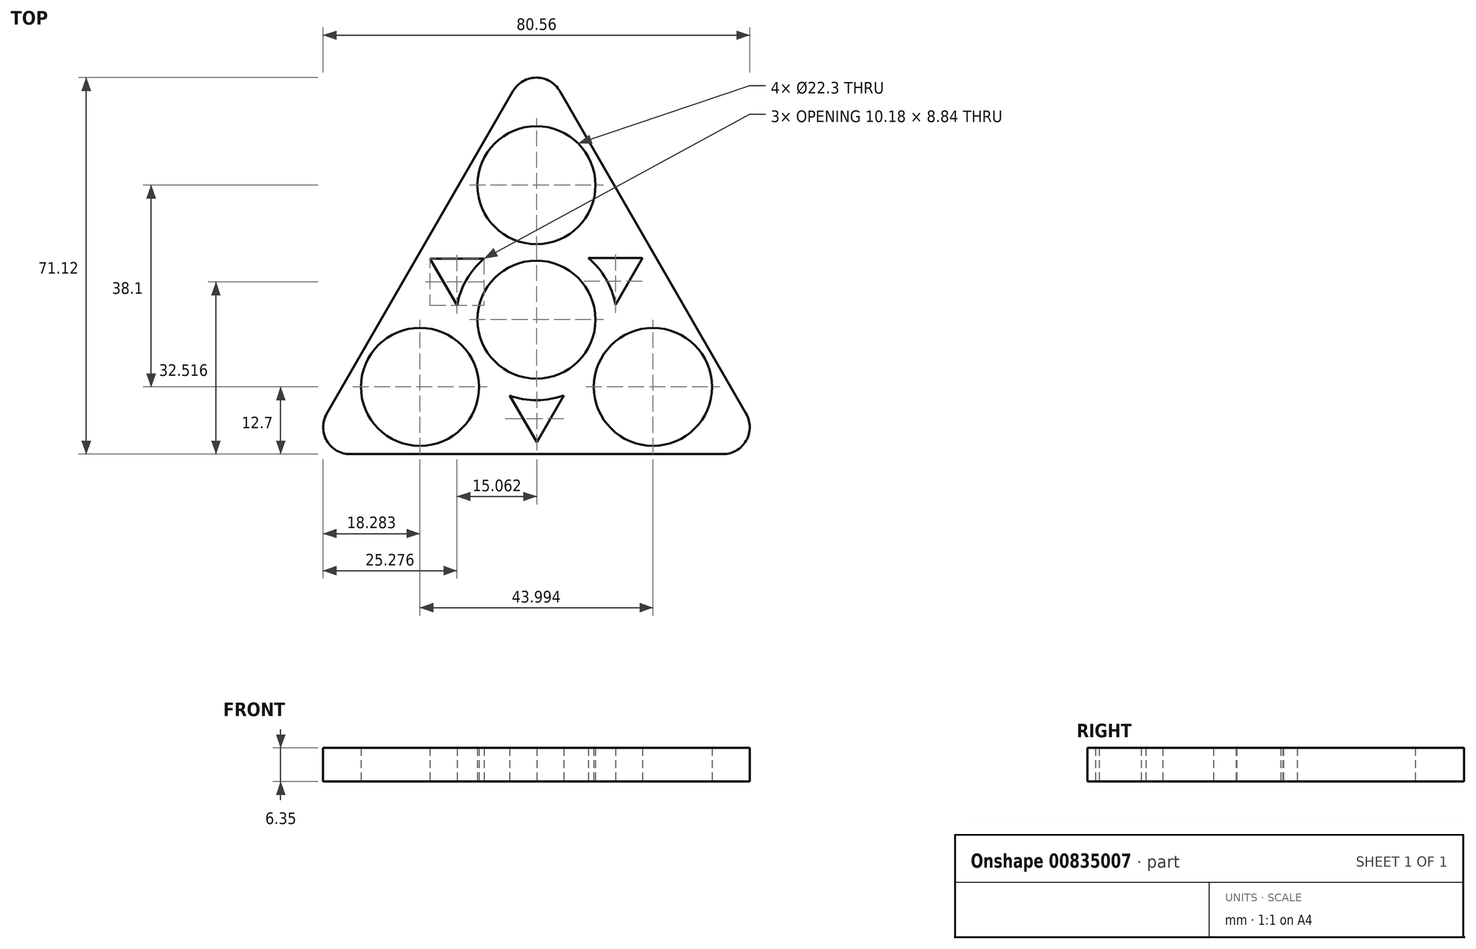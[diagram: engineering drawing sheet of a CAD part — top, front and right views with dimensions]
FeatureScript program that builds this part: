
annotation { "Feature Type Name" : "Feature", "Feature Type Description" : "" }
export const myFeature = defineFeature(function(context is Context, id is Id, definition is map)
    precondition{}
    {
        {
            var Q0;
            Q0=qCreatedBy(makeId("Top.planeOp"),FACE);
            var sketch = newSketch(context, id + "F0", { "sketchPlane" : qUnion([Q0])});
            skCircle(sketch, "E0.cCircle", {"center": v(0, 0) * mm, "radius": 25.4 * mm, "construction": true});
            skLineSegment(sketch, "E0.0", {"start": v(0, 50.8) * mm, "end": v(44, -25.4) * mm});
            skLineSegment(sketch, "E0.1", {"start": v(44, -25.4) * mm, "end": v(-44, -25.4) * mm});
            skLineSegment(sketch, "E0.2", {"start": v(-44, -25.4) * mm, "end": v(0, 50.8) * mm});
            skPoint(sketch, "E0.0.midPoint", {"position": v(22, 12.7) * mm});
            skCircle(sketch, "E1.cCircle", {"center": v(0, 0) * mm, "radius": 11.15 * mm, "construction": true});
            skCircle(sketch, "E2", {"center": v(0, 0) * mm, "radius": 11.15 * mm});
            skCircle(sketch, "E3", {"center": v(0, 25.4) * mm, "radius": 11.15 * mm});
            skCircle(sketch, "E4.cCircle", {"center": v(0, 0) * mm, "radius": 12.7 * mm, "construction": true});
            skPoint(sketch, "E4.0.midPoint", {"position": v(11, -6.35) * mm});
            skCircle(sketch, "E5", {"center": v(-22, -12.7) * mm, "radius": 11.15 * mm});
            skCircle(sketch, "E6", {"center": v(22, -12.7) * mm, "radius": 11.15 * mm});
            skCircle(sketch, "E7", {"center": v(0, 0) * mm, "radius": 15.2 * mm});
            skCircle(sketch, "E8.cCircle", {"center": v(0, 0) * mm, "radius": 11.58 * mm, "construction": true});
            skLineSegment(sketch, "E8.0", {"start": v(-20.1, 11.5) * mm, "end": v(20, 11.66) * mm});
            skLineSegment(sketch, "E8.1", {"start": v(20, 11.66) * mm, "end": v(0.1, -23.15) * mm});
            skLineSegment(sketch, "E8.2", {"start": v(0.1, -23.15) * mm, "end": v(-20.1, 11.5) * mm});
            skPoint(sketch, "E8.0.midPoint", {"position": v(-0.05, 11.58) * mm});
            skSolve(sketch);
        }
        {
            var Q0;
            {var subQ3=sQuery(id+"F0.wireOp",EDGE,"E7");var subQ5=sQuery(id+"F0.wireOp",EDGE,"E3");var subQ6=makeQuery(id+"F0.imprint","INTERSECT",VERTEX,{"disambiguationData":[OD(0.0)],"derivedFrom":[subQ5,subQ3]});Q0=makeQuery(id+"F0.imprint","IMPRINT",FACE,{"disambiguationData":[TD([[makeQuery(id+"F0.imprint","IMPRINT",EDGE,{"disambiguationData":[TD([[subQ6,-1.0]])],"derivedFrom":subQ5}),-1.0]])]});}
            var Q1;
            {var subQ0=sQuery(id+"F0.wireOp",EDGE,"E7");var subQ1=sQuery(id+"F0.wireOp",EDGE,"E6");var subQ2=makeQuery(id+"F0.imprint","INTERSECT",VERTEX,{"disambiguationData":[OD(0.0)],"derivedFrom":[subQ1,subQ0]});Q1=makeQuery(id+"F0.imprint","IMPRINT",FACE,{"disambiguationData":[TD([[makeQuery(id+"F0.imprint","IMPRINT",EDGE,{"disambiguationData":[TD([[subQ2,-1.0]])],"derivedFrom":subQ1}),-1.0]])]});}
            var Q2;
            {var subQ0=sQuery(id+"F0.wireOp",EDGE,"E7");var subQ1=sQuery(id+"F0.wireOp",EDGE,"E5");var subQ2=makeQuery(id+"F0.imprint","INTERSECT",VERTEX,{"disambiguationData":[OD(0.0)],"derivedFrom":[subQ1,subQ0]});Q2=makeQuery(id+"F0.imprint","IMPRINT",FACE,{"disambiguationData":[TD([[makeQuery(id+"F0.imprint","IMPRINT",EDGE,{"disambiguationData":[TD([[subQ2,-1.0]])],"derivedFrom":subQ1}),-1.0]])]});}
            extrude(context, id + "F1", {"entities" : qUnion([Q0, Q1, Q2]), "depth" : 6.35 * mm, "offsetDistance" : 25.4 * mm});
        }
        {
            var Q0;
            {var subQ0=sQuery(id+"F0.wireOp",EDGE,"E7");var subQ1=sQuery(id+"F0.wireOp",EDGE,"E6");var subQ2=makeQuery(id+"F0.imprint","INTERSECT",VERTEX,{"disambiguationData":[OD(0.0)],"derivedFrom":[subQ1,subQ0]});Q0=makeQuery(id+"F0.imprint","IMPRINT",FACE,{"disambiguationData":[TD([[makeQuery(id+"F0.imprint","IMPRINT",EDGE,{"disambiguationData":[TD([[subQ2,1.0]])],"derivedFrom":subQ1}),-1.0]])]});}
            var Q1;
            {var subQ0=sQuery(id+"F0.wireOp",EDGE,"E7");var subQ1=sQuery(id+"F0.wireOp",EDGE,"E3");var subQ2=makeQuery(id+"F0.imprint","INTERSECT",VERTEX,{"disambiguationData":[OD(0.0)],"derivedFrom":[subQ1,subQ0]});Q1=makeQuery(id+"F0.imprint","IMPRINT",FACE,{"disambiguationData":[TD([[makeQuery(id+"F0.imprint","IMPRINT",EDGE,{"disambiguationData":[TD([[subQ2,1.0]])],"derivedFrom":subQ1}),-1.0]])]});}
            var Q2;
            {var subQ0=sQuery(id+"F0.wireOp",EDGE,"E7");var subQ1=sQuery(id+"F0.wireOp",EDGE,"E5");var subQ2=makeQuery(id+"F0.imprint","INTERSECT",VERTEX,{"disambiguationData":[OD(0.0)],"derivedFrom":[subQ1,subQ0]});Q2=makeQuery(id+"F0.imprint","IMPRINT",FACE,{"disambiguationData":[TD([[makeQuery(id+"F0.imprint","IMPRINT",EDGE,{"disambiguationData":[TD([[subQ2,1.0]])],"derivedFrom":subQ1}),-1.0]])]});}
            var Q3;
            Q3=makeQuery(id+"F0.imprint","IMPRINT",FACE,{"disambiguationData":[TD([[makeQuery(id+"F0.imprint","IMPRINT",EDGE,{"derivedFrom":sQuery(id+"F0.wireOp",EDGE,"E2")}),-1.0]])]});
            extrude(context, id + "F2", {"entities" : qUnion([Q0, Q1, Q2, Q3]), "operationType" : NewBodyOperationType.ADD, "depth" : 6.35 * mm, "offsetDistance" : 25.4 * mm});
        }
        {
            var Q0;
            Q0=makeQuery(id+"F1.opExtrude","SWEPT_EDGE",EDGE,{"disambiguationData":[OSD([sQuery(id+"F0.wireOp",EDGE,"E0.0"),sQuery(id+"F0.wireOp",EDGE,"E0.2")])]});
            var Q1;
            Q1=makeQuery(id+"F1.opExtrude","SWEPT_EDGE",EDGE,{"disambiguationData":[OSD([sQuery(id+"F0.wireOp",EDGE,"E0.0"),sQuery(id+"F0.wireOp",EDGE,"E0.1")])]});
            var Q2;
            Q2=makeQuery(id+"F1.opExtrude","SWEPT_EDGE",EDGE,{"disambiguationData":[OSD([sQuery(id+"F0.wireOp",EDGE,"E0.1"),sQuery(id+"F0.wireOp",EDGE,"E0.2")])]});
            fillet(context, id + "F3", {"entities" : qUnion([Q0, Q1, Q2]), "radius" : 5.08 * mm, "tangentPropagation" : true, "allowEdgeOverflow" : false});
        }
    });
